# Revit family: Wave Family
name_source: partatom
category: Furniture
revit_build: Autodesk Revit 2018 (Build: 20170223_1515(x64)
units: mm (PartAtom-declared; Revit-internal decimal feet)

## family parameters
Always vertical = Yes
Cut with Voids When Loaded = No
OmniClass Number = 23.40.20.00
OmniClass Title = General Furniture and Specialties
Room Calculation Point = No
Shared = No
Work Plane-Based = No

## types (9) — shared parameters

## per-type parameters (varying)
| type | Furniture Type |
| Table Rectangular (1800X900X730) | Wave Range Family : Table 1800X900X730 |
| Table Rectangular (2000X1000X730) | Wave Range Family : Table 2000X1000X730 |
| Table Rectangular (2400X1000X730) | Wave Range Family : Table 2400X1000X730 |
| Bench Rectangular (1600X400X440X440) | Wave Range Family : Bench 1600X400X440 |
| Bench Rectangular (1800X400X440X440) | Wave Range Family : Bench 1800X400X440 |
| Bench Rectangular (2200X400X440X440) | Wave Range Family : Bench 2200X400X440 |
| Round Table (1050X1050X730) | Wave Range Family : Round Table 1050X1050X730 |
| Round Table (1200X1200X730) | Wave Range Family : Round Table 1200X1200X730 |
| Bench Curved (1300X550X400X440) | Wave Curve Family : Curved Bench (1300X550X400X440) |

## geometry (parser evidence)
native form markers: Sweep x53
no freeform markers — native parametric forms only
